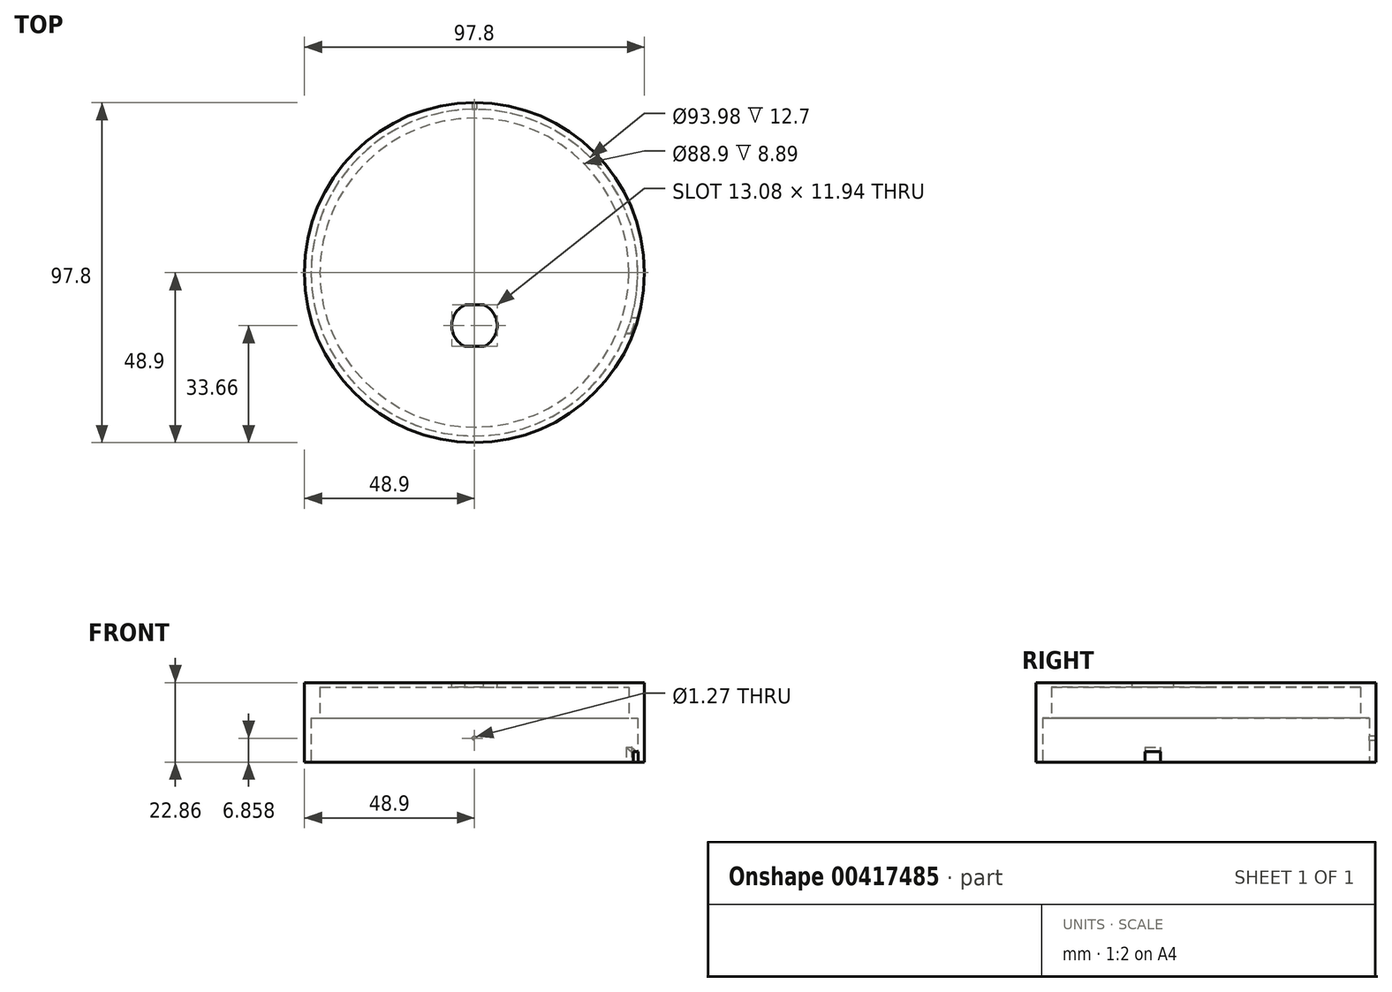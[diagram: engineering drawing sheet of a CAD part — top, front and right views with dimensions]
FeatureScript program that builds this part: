
annotation { "Feature Type Name" : "Feature", "Feature Type Description" : "" }
export const myFeature = defineFeature(function(context is Context, id is Id, definition is map)
    precondition{}
    {
        {
            var Q0;
            Q0=qCreatedBy(makeId("Top.planeOp"),FACE);
            var sketch = newSketch(context, id + "F0", { "sketchPlane" : qUnion([Q0])});
            skCircle(sketch, "E0", {"center": v(0, 0) * mm, "radius": 48.9 * mm});
            skSolve(sketch);
        }
        {
            var Q0;
            Q0 = qSketchRegion(id + "F0", true);
            extrude(context, id + "F1", {"entities" : qUnion([Q0]), "oppositeDirection" : true, "depth" : 22.86 * mm});
        }
        {
            var Q0;
            Q0=qCreatedBy(makeId("Top.planeOp"),FACE);
            var sketch = newSketch(context, id + "F2", { "sketchPlane" : qUnion([Q0])});
            skLineSegment(sketch, "E1", {"start": v(0, 10.35) * mm, "end": v(0, -44.57) * mm, "construction": true});
            skLineSegment(sketch, "E2", {"start": v(-11.93, -15.24) * mm, "end": v(19.98, -15.24) * mm, "construction": true});
            skArc(sketch, "E3", {"start": v(2.67, -21.2) * mm, "mid": v(6.54, -15.24) * mm, "end": v(2.67, -9.27) * mm});
            skLineSegment(sketch, "E4.bottom", {"start": v(2.67, -9.27) * mm, "end": v(-2.67, -9.27) * mm});
            skLineSegment(sketch, "E4.top", {"start": v(2.67, -21.2) * mm, "end": v(-2.67, -21.2) * mm});
            skPoint(sketch, "E5.orphan", {"position": v(-5.78, -9.27) * mm});
            skPoint(sketch, "E6.orphan", {"position": v(-5.97, -21.2) * mm});
            skPoint(sketch, "E7.orphan", {"position": v(5.78, -21.2) * mm});
            skPoint(sketch, "E8.orphan", {"position": v(5.97, -9.27) * mm});
            skArc(sketch, "E9.trimOffspring", {"start": v(-2.67, -9.27) * mm, "mid": v(-6.54, -15.24) * mm, "end": v(-2.67, -21.2) * mm});
            skSolve(sketch);
        }
        {
            var Q0;
            Q0 = qSketchRegion(id + "F2", true);
            extrude(context, id + "F3", {"entities" : qUnion([Q0]), "operationType" : NewBodyOperationType.REMOVE, "endBound" : BoundingType.THROUGH_ALL, "oppositeDirection" : true, "depth" : 25.4 * mm});
        }
        {
            var Q0;
            Q0=makeQuery(id+"F1.opExtrude","CAP_FACE",FACE,{"disambiguationData":[OSD([sQuery(id+"F0.wireOp",EDGE,"E0")])],"isStart":false});
            cPlane(context, id + "F4", {"entities" : qUnion([Q0]), "cplaneType" : CPlaneType.OFFSET, "offset" : 0 * mm, "width" : 152.4 * mm, "height" : 152.4 * mm});
        }
        {
            var Q0;
            Q0=qCreatedBy(id+"F4.planeOp",FACE);
            var sketch = newSketch(context, id + "F5", { "sketchPlane" : qUnion([Q0])});
            skCircle(sketch, "E10", {"center": v(0, 0) * mm, "radius": 47 * mm});
            skSolve(sketch);
        }
        {
            var Q0;
            Q0 = qSketchRegion(id + "F5", true);
            extrude(context, id + "F6", {"entities" : qUnion([Q0]), "operationType" : NewBodyOperationType.REMOVE, "oppositeDirection" : true, "depth" : 12.7 * mm});
        }
        {
            var Q0;
            Q0=qCreatedBy(id+"F4.planeOp",FACE);
            var sketch = newSketch(context, id + "F7", { "sketchPlane" : qUnion([Q0])});
            skCircle(sketch, "E11", {"center": v(0, 0) * mm, "radius": 44.45 * mm});
            skSolve(sketch);
        }
        {
            var Q0;
            Q0 = qSketchRegion(id + "F7", true);
            extrude(context, id + "F8", {"entities" : qUnion([Q0]), "operationType" : NewBodyOperationType.REMOVE, "oppositeDirection" : true, "depth" : 21.59 * mm});
        }
        {
            var Q0;
            Q0=qCreatedBy(makeId("Right.planeOp"),FACE);
            var sketch = newSketch(context, id + "F9", { "sketchPlane" : qUnion([Q0])});
            skLineSegment(sketch, "E12", {"start": v(-15.24, 3.43) * mm, "end": v(-15.24, -42.89) * mm, "construction": true});
            skLineSegment(sketch, "E13.bottom", {"start": v(-17.46, -22.86) * mm, "end": v(-13.02, -22.86) * mm});
            skLineSegment(sketch, "E13.top", {"start": v(-17.46, -19.81) * mm, "end": v(-13.02, -19.81) * mm});
            skLineSegment(sketch, "E13.left", {"start": v(-17.46, -22.86) * mm, "end": v(-17.46, -19.81) * mm});
            skLineSegment(sketch, "E13.right", {"start": v(-13.02, -22.86) * mm, "end": v(-13.02, -19.81) * mm});
            skPoint(sketch, "E13.middle", {"position": v(-15.24, -21.34) * mm});
            skSolve(sketch);
        }
        {
            var Q0;
            Q0 = qSketchRegion(id + "F9", true);
            extrude(context, id + "F10", {"entities" : qUnion([Q0]), "operationType" : NewBodyOperationType.REMOVE, "endBound" : BoundingType.THROUGH_ALL, "depth" : 25.4 * mm});
        }
        {
            var Q0;
            Q0=makeQuery(id+"F10.boolean.opBoolean","INTERSECT",EDGE,{"derivedFrom":[makeQuery(id+"F6.boolean.opBoolean","COPY",FACE,{"derivedFrom":makeQuery(id+"F6.opExtrude","SWEPT_FACE",FACE,{"disambiguationData":[OSD([sQuery(id+"F5.wireOp",EDGE,"E10")])]})}),makeQuery(id+"F10.opExtrude","SWEPT_FACE",FACE,{"disambiguationData":[OSD([sQuery(id+"F9.wireOp",EDGE,"E13.top")])]})]});
            chamfer(context, id + "F11", {"entities" : qUnion([Q0]), "width" : 1.27 * mm, "tangentPropagation" : true});
        }
        {
            var Q0;
            Q0=qCreatedBy(makeId("Front.planeOp"),FACE);
            var sketch = newSketch(context, id + "F12", { "sketchPlane" : qUnion([Q0])});
            skLineSegment(sketch, "E14", {"start": v(0, 11.62) * mm, "end": v(0, -51.27) * mm, "construction": true});
            skLineSegment(sketch, "E15", {"start": v(16.2, -16) * mm, "end": v(-26.52, -16) * mm, "construction": true});
            skCircle(sketch, "E16", {"center": v(0, -16) * mm, "radius": 0.64 * mm});
            skSolve(sketch);
        }
        {
            var Q0;
            Q0 = qSketchRegion(id + "F12", true);
            extrude(context, id + "F13", {"entities" : qUnion([Q0]), "operationType" : NewBodyOperationType.REMOVE, "endBound" : BoundingType.THROUGH_ALL, "oppositeDirection" : true, "depth" : 25.4 * mm});
        }
    });
